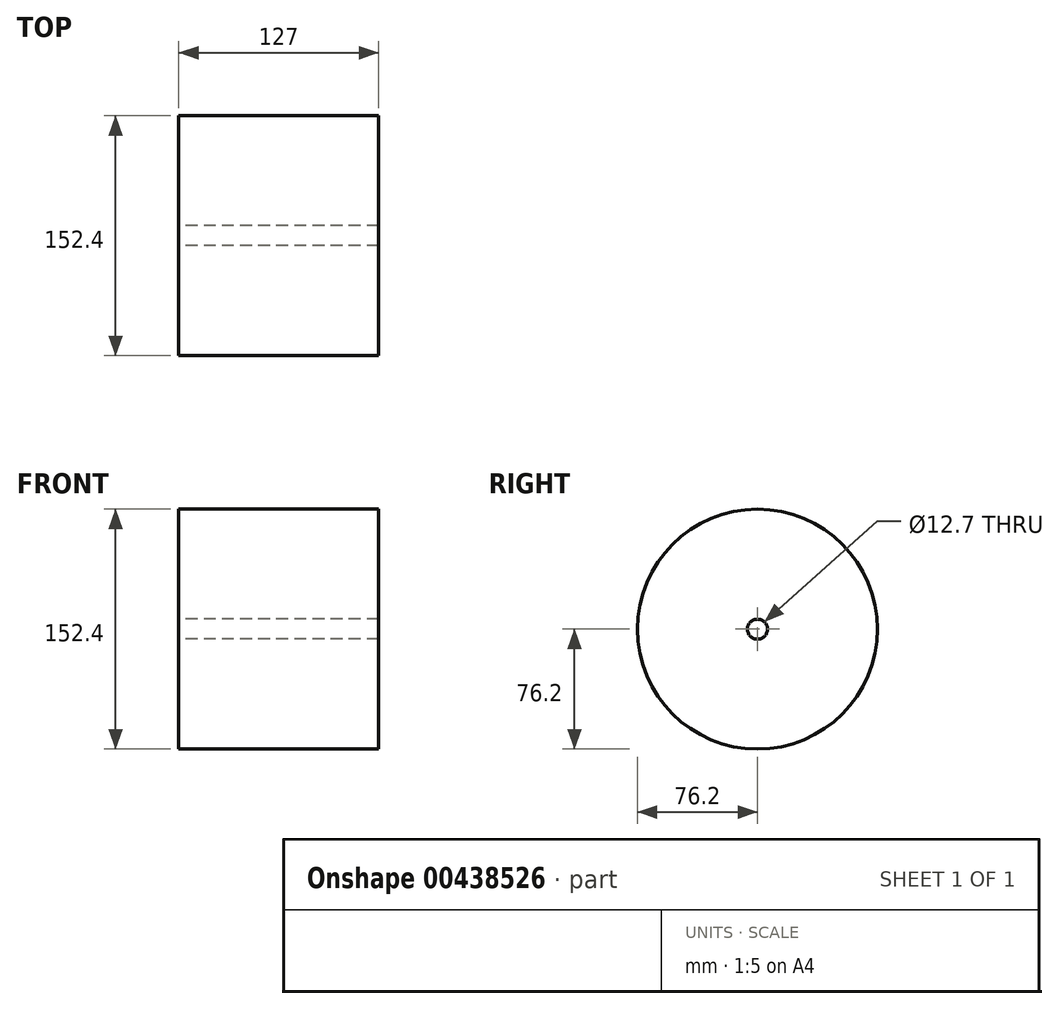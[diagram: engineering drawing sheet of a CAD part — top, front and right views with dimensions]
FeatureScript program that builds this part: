
annotation { "Feature Type Name" : "Feature", "Feature Type Description" : "" }
export const myFeature = defineFeature(function(context is Context, id is Id, definition is map)
    precondition{}
    {
        {
            var Q0;
            Q0=qCreatedBy(makeId("Right.planeOp"),FACE);
            var sketch = newSketch(context, id + "F0", { "sketchPlane" : qUnion([Q0])});
            skCircle(sketch, "E0", {"center": v(0, 0) * mm, "radius": 76.2 * mm});
            skCircle(sketch, "E1", {"center": v(0, 0) * mm, "radius": 6.35 * mm});
            skSolve(sketch);
        }
        {
            var Q0;
            Q0 = qSketchRegion(id + "F0", true);
            extrude(context, id + "F1", {"entities" : qUnion([Q0]), "depth" : 127 * mm});
        }
    });
